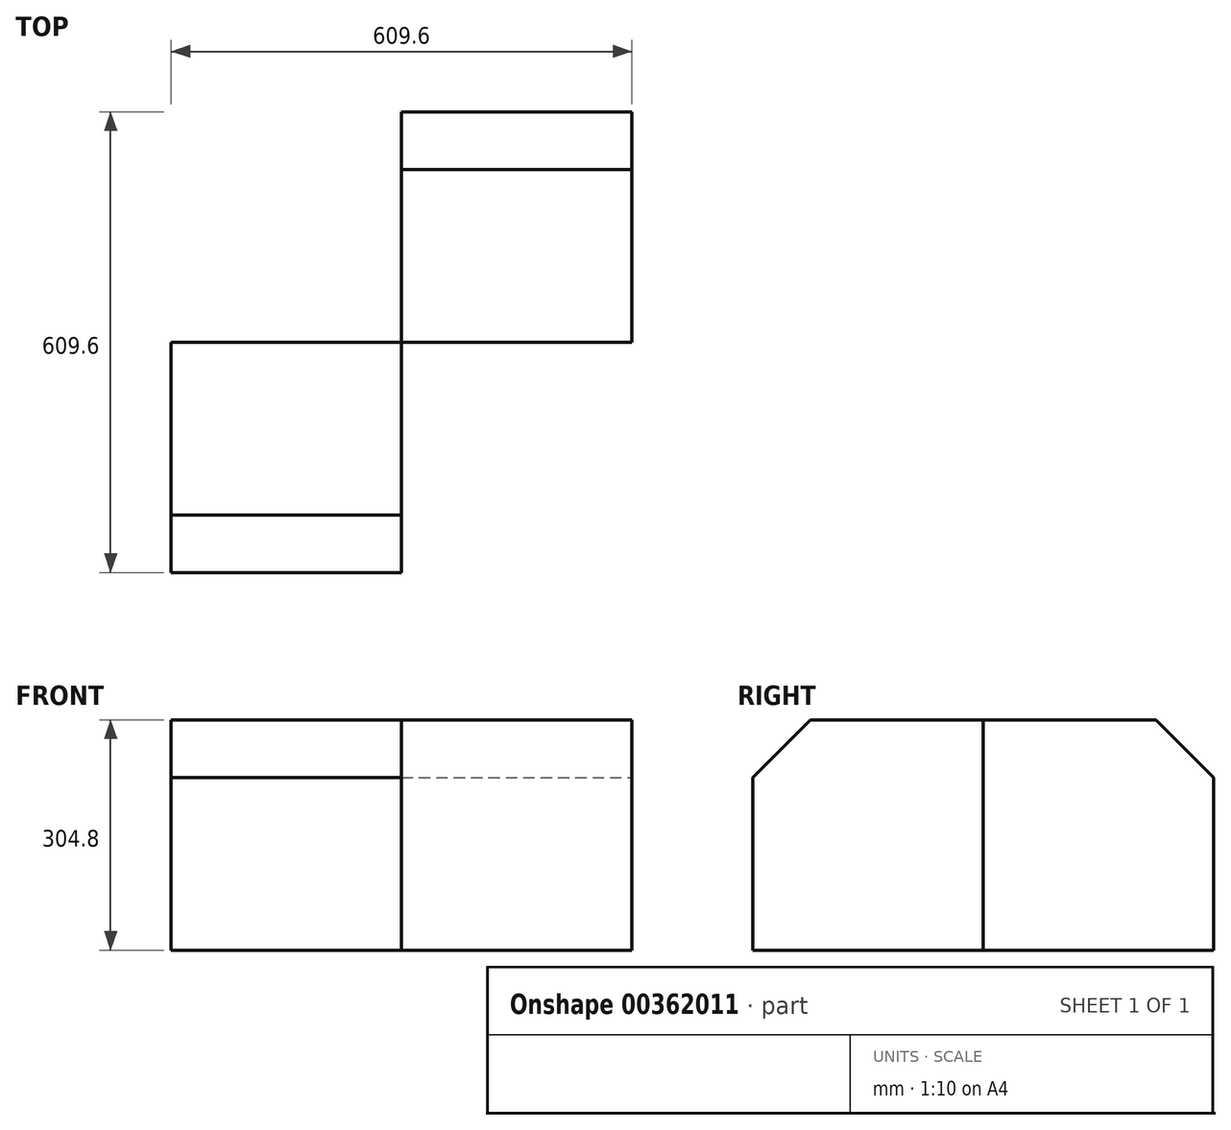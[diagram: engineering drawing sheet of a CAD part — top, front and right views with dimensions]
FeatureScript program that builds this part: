
annotation { "Feature Type Name" : "Feature", "Feature Type Description" : "" }
export const myFeature = defineFeature(function(context is Context, id is Id, definition is map)
    precondition{}
    {
        {
            var Q0;
            Q0=qCreatedBy(makeId("Front.planeOp"),FACE);
            var sketch = newSketch(context, id + "F0", { "sketchPlane" : qUnion([Q0])});
            skLineSegment(sketch, "E0.bottom", {"start": v(0, 304.8) * mm, "end": v(304.8, 304.8) * mm});
            skLineSegment(sketch, "E0.top", {"start": v(0, 0) * mm, "end": v(304.8, 0) * mm});
            skLineSegment(sketch, "E0.left", {"start": v(0, 304.8) * mm, "end": v(0, 0) * mm});
            skLineSegment(sketch, "E0.right", {"start": v(304.8, 304.8) * mm, "end": v(304.8, 0) * mm});
            skSolve(sketch);
        }
        {
            var Q0;
            Q0=makeQuery(id+"F0.imprint","IMPRINT",FACE,{"disambiguationData":[TD([[makeQuery(id+"F0.imprint","IMPRINT",EDGE,{"derivedFrom":sQuery(id+"F0.wireOp",EDGE,"E0.bottom")}),-1.0]])]});
            extrude(context, id + "F1", {"entities" : qUnion([Q0]), "depth" : 304.8 * mm});
        }
        {
            var Q0;
            Q0=makeQuery(id+"F1.opExtrude","CAP_EDGE",EDGE,{"disambiguationData":[OSD([sQuery(id+"F0.wireOp",EDGE,"E0.bottom")])],"isStart":false});
            chamfer(context, id + "F2", {"entities" : qUnion([Q0]), "width" : 76.2 * mm, "tangentPropagation" : true});
        }
        {
            var Q0;
            Q0=makeQuery(id+"F1.opExtrude","SWEPT_BODY",BODY,{"disambiguationData":[OSD([sQuery(id+"F0.wireOp",EDGE,"E0.bottom"),sQuery(id+"F0.wireOp",EDGE,"E0.top"),sQuery(id+"F0.wireOp",EDGE,"E0.left"),sQuery(id+"F0.wireOp",EDGE,"E0.right")])]});
            var Q1;
            Q1=makeQuery(id+"F1.opExtrude","CAP_EDGE",EDGE,{"disambiguationData":[OSD([sQuery(id+"F0.wireOp",EDGE,"E0.right")])],"isStart":true});
            transform(context, id + "F3", {"entities" : qUnion([Q0]), "transformType" : TransformType.ROTATION, "transformAxis" : qUnion([Q1]), "angle" : 180 * degree, "makeCopy" : true});
        }
    });
